# Revit family: Outside FlexiElectric 210x210cm 30-49210-210
name_source: partatom
category: Specialty Equipment
units: mm (PartAtom-declared; Revit-internal decimal feet)

## family parameters
Always vertical = Yes
Cut with Voids When Loaded = No
Enable Cutting in Views = Yes
Maintain Annotation Orientation = No
OmniClass Number = 23.40.00.00
OmniClass Title = Equipment and Furnishings
Part Type = Normal
Room Calculation Point = No
Round Connector Dimension = Use Diameter
Shared = No
Work Plane-Based = No

## types (1)
- Standard
    Cost Center = 0 g
    Default Elevation = 0 mm  [stored 0 ft]
    Description = Outside FlexiEl Corner 210x210cm
    Design State = 1
    Designer = sj
    L = 1 mm  [stored 0.00328084 ft]
    Length = 0*10
    Malermeter = 111.005552
    Manufacturer = Ropox
    Model = 30-49210-210
    Part Number = 30-49210-210_Simplify_1
    SaveDate = 16-07-2008
    SaveTime = 09:39
    Width = 0*10

note: [stored X ft] marks values corroborated as IEEE doubles in the binary element streams (Revit-internal decimal feet)

## geometry (parser evidence)
native form markers: Sweep x3
no freeform markers — native parametric forms only
